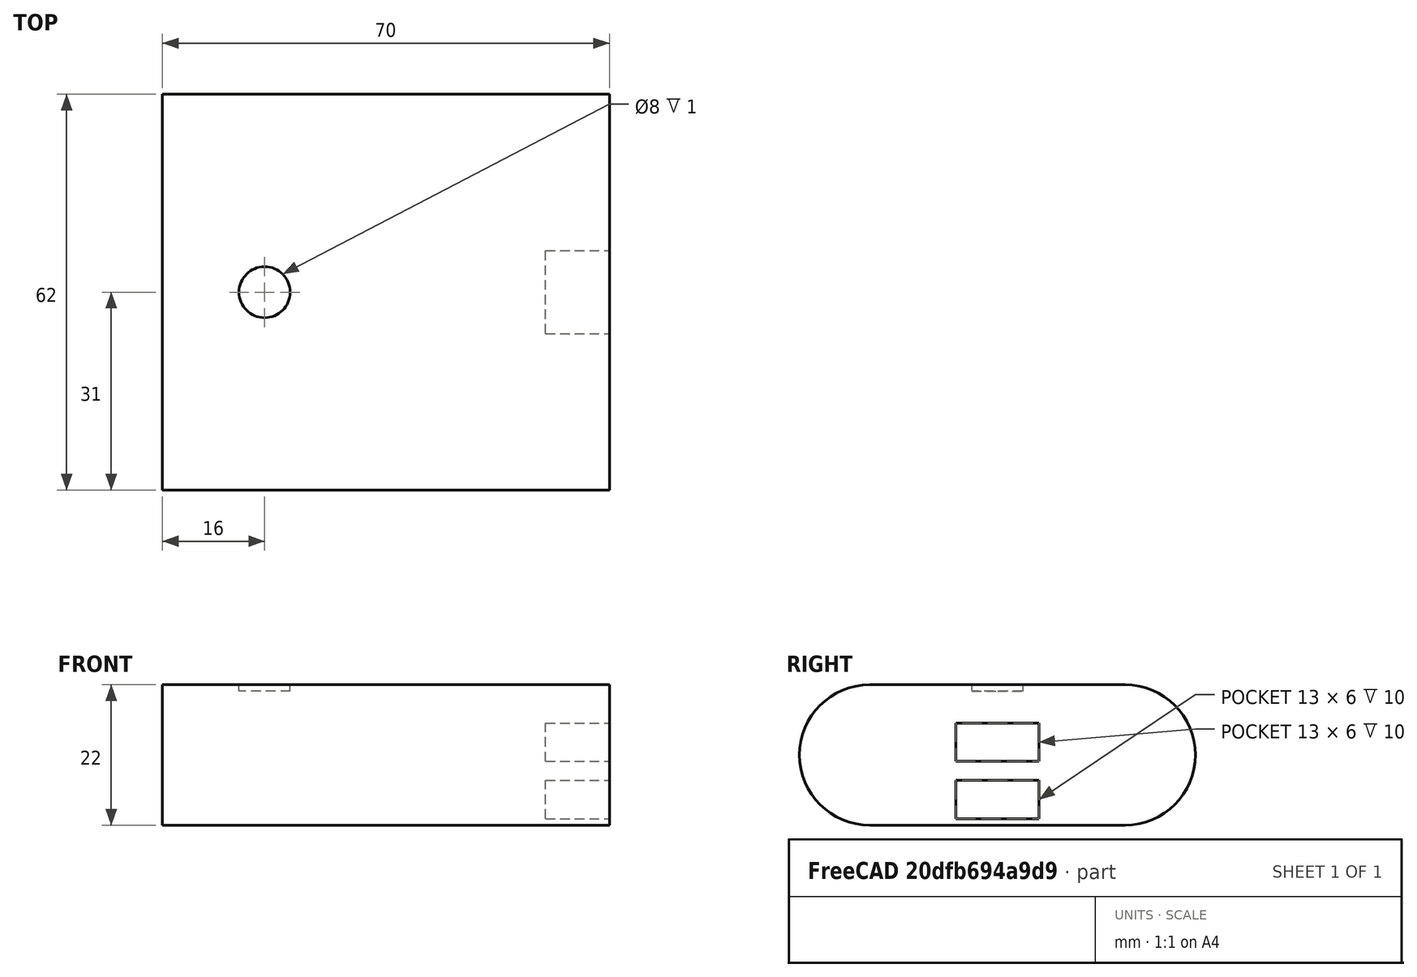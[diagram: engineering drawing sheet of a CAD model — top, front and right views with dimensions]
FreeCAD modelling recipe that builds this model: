
FCSTD DOCUMENT
Label: Eneloop
objects: Part::Box×3, Part::Cylinder×3, Part::MultiFuse×2, Part::Cut×1
note: 9 computed .brp shape members not serialized (recipe doc carries the construction recipe); baked Part::Feature solids carry a one-line shape summary decoded from their .brp

FEATURE [Part::Box] Box
  Height = 22
  Length = 70
  Placement = pos=(0,0,-11) rot=(0,0,1;0rad)
  Width = 40
FEATURE [Part::Cylinder] Cylinder
  Angle = 360
  Height = 70
  Placement = pos=(0,0,0) rot=(0,1,0;1.5708rad)
  Radius = 11
FEATURE [Part::Cylinder] Cylinder001
  Angle = 360
  Height = 70
  Placement = pos=(0,40,0) rot=(0,1,0;1.5708rad)
  Radius = 11
FEATURE [Part::Cylinder] Cylinder002  label="PowerButton"
  Angle = 360
  Height = 2
  Placement = pos=(16,20,10) rot=(0,0,1;0rad)
  Radius = 4
FEATURE [Part::Box] Box001  label="USB1"
  Height = 6
  Length = 15
  Placement = pos=(60,13.5,-1) rot=(0,0,1;0rad)
  Width = 13
FEATURE [Part::Box] Box001001  label="USB2"
  Height = 6
  Length = 15
  Placement = pos=(60,13.5,-10) rot=(0,0,1;0rad)
  Width = 13
FEATURE [Part::MultiFuse] Fusion
  Shapes = -> [Cylinder001,Box,Cylinder]
FEATURE [Part::MultiFuse] Fusion001
  Shapes = -> [Box001001,Cylinder002,Box001]
FEATURE [Part::Cut] Cut  label="Eneloop"
  Base = -> Fusion
  Tool = -> Fusion001
